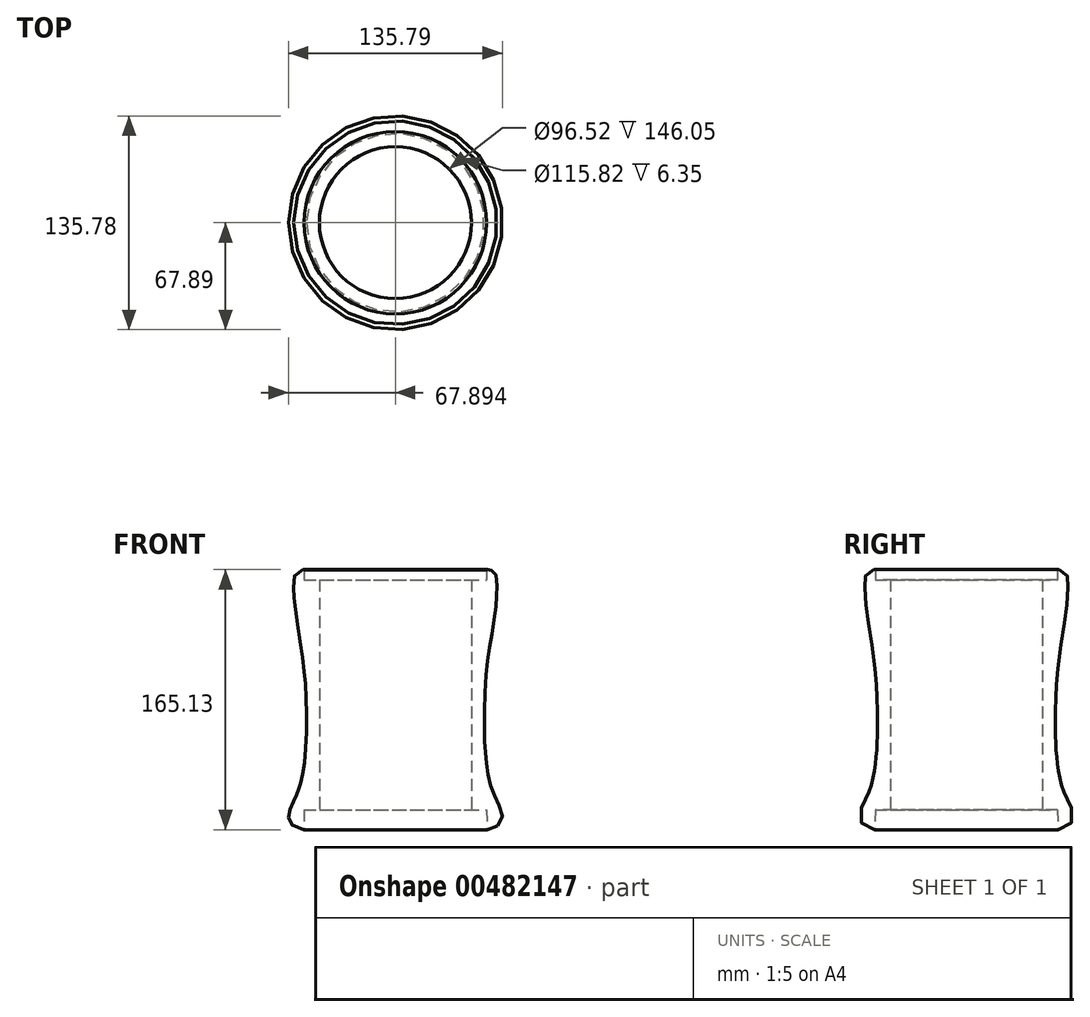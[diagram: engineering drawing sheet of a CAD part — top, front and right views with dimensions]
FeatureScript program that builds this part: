
annotation { "Feature Type Name" : "Feature", "Feature Type Description" : "" }
export const myFeature = defineFeature(function(context is Context, id is Id, definition is map)
    precondition{}
    {
        {
            var Q0;
            Q0=qCreatedBy(makeId("Front.planeOp"),FACE);
            var sketch = newSketch(context, id + "F0", { "sketchPlane" : qUnion([Q0])});
            skLineSegment(sketch, "E0", {"start": v(-1.03, -95.24) * mm, "end": v(8.62, -95.24) * mm});
            skLineSegment(sketch, "E1", {"start": v(8.62, -95.24) * mm, "end": v(8.62, 50.81) * mm});
            skLineSegment(sketch, "E2", {"start": v(8.62, 50.81) * mm, "end": v(-1.03, 50.81) * mm});
            skLineSegment(sketch, "E3", {"start": v(-1.03, 50.81) * mm, "end": v(-1.03, 57.16) * mm});
            skLineSegment(sketch, "E4", {"start": v(-1.03, -95.24) * mm, "end": v(-1.26, -107.94) * mm});
            skFitSpline(sketch, "E5", {"points": [v(-1.03, 57.16) * mm, v(-7.73, 47.04) * mm, v(-6.6, 31.7) * mm, v(-1.88, 0) * mm, v(0, -21.73) * mm, v(0, -56.1) * mm, v(-2.48, -75.3) * mm, v(-4.28, -81.98) * mm, v(-5.85, -85.75) * mm, v(-8.94, -92.35) * mm, v(-10.97, -100.48) * mm, v(-1.26, -107.94) * mm], "startDerivative": vector(-240.86, 17.2) * mm, "endDerivative": vector(250.61, -35.53) * mm});
            skLineSegment(sketch, "E6", {"start": v(8.62, -95.24) * mm, "end": v(56.88, -95.24) * mm, "construction": true});
            skLineSegment(sketch, "E7", {"start": v(56.88, -95.24) * mm, "end": v(56.88, 37.6) * mm, "construction": true});
            skSolve(sketch);
        }
        {
            var Q0;
            Q0=makeQuery(id+"F0.imprint","IMPRINT",FACE,{"disambiguationData":[TD([[makeQuery(id+"F0.imprint","IMPRINT",EDGE,{"derivedFrom":sQuery(id+"F0.wireOp",EDGE,"E0")}),1.0]])]});
            var Q1;
            Q1=sQuery(id+"F0.wireOp",EDGE,"E7");
            revolve(context, id + "F1", {"entities" : qUnion([Q0]), "axis" : qUnion([Q1]), "revolveType" : RevolveType.FULL});
        }
    });
